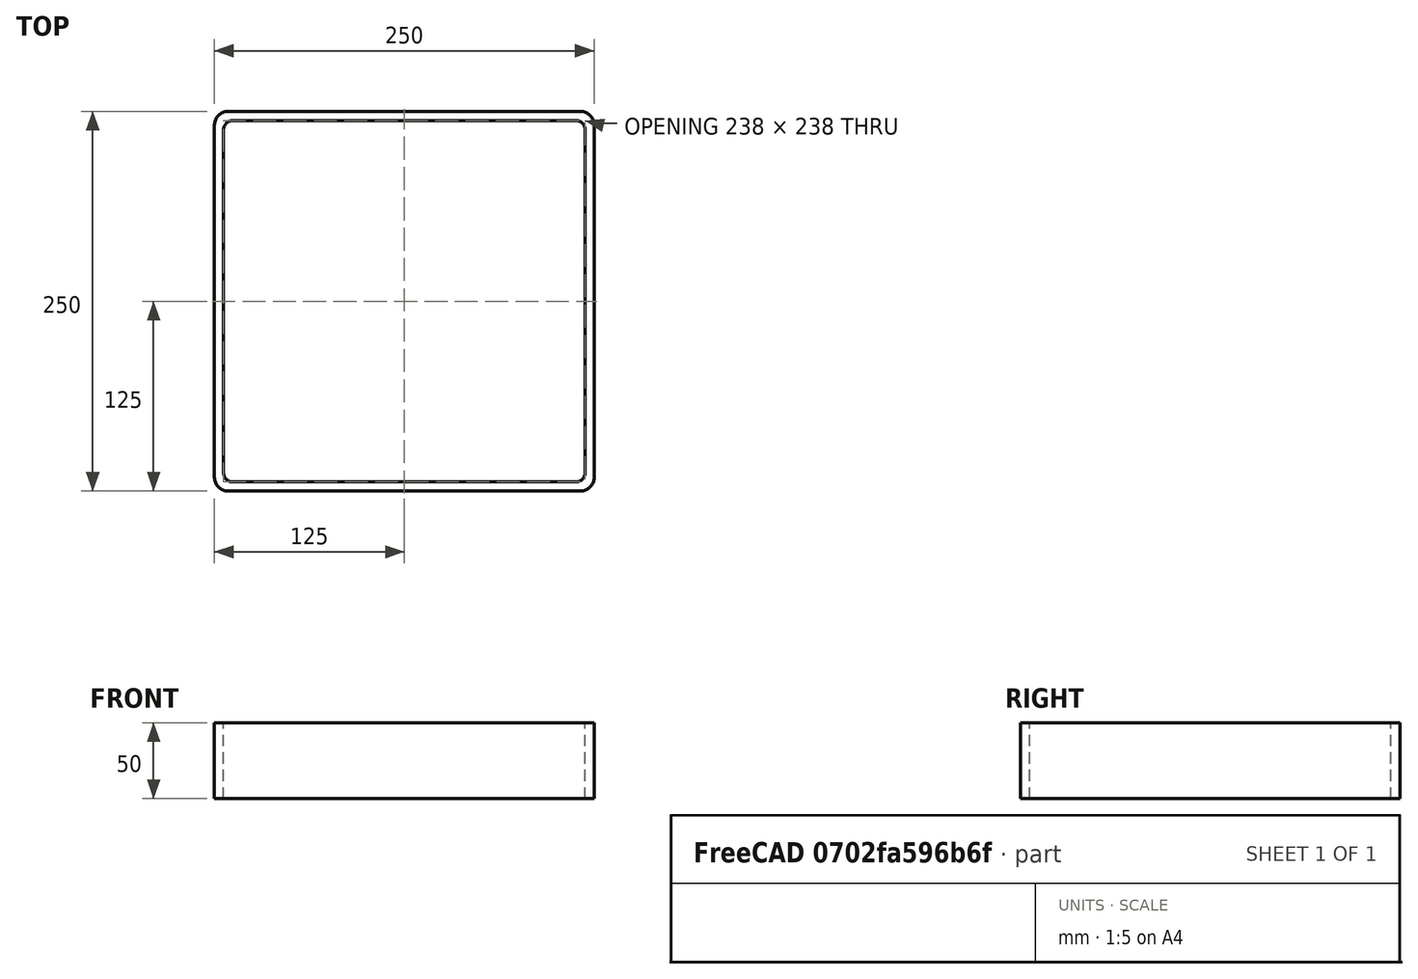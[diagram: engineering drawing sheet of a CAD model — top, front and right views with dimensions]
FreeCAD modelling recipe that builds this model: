
FCSTD DOCUMENT  (FreeCAD 0.15R4671 (Git))
Label: Square hollow section 250x250x6 EN10219 S235JRH
License: All rights reserved
LicenseURL: http://en.wikipedia.org/wiki/All_rights_reserved
objects: Sketcher::SketchObject×1, Part::Extrusion×1
note: 2 computed .brp shape members not serialized (recipe doc carries the construction recipe); baked Part::Feature solids carry a one-line shape summary decoded from their .brp

FEATURE [Sketcher::SketchObject] Sketch
  sketch-geometry (16):
    g0: LineSegment StartX=-113 StartY=119 StartZ=0 EndX=113 EndY=119 EndZ=0
    g1: LineSegment StartX=119 StartY=113 StartZ=0 EndX=119 EndY=-113 EndZ=0
    g2: LineSegment StartX=113 StartY=-119 StartZ=0 EndX=-113 EndY=-119 EndZ=0
    g3: LineSegment StartX=-119 StartY=-113 StartZ=0 EndX=-119 EndY=113 EndZ=0
    g4: LineSegment StartX=-116 StartY=125 StartZ=0 EndX=116 EndY=125 EndZ=0
    g5: LineSegment StartX=125 StartY=116 StartZ=0 EndX=125 EndY=-116 EndZ=0
    g6: LineSegment StartX=116 StartY=-125 StartZ=0 EndX=-116 EndY=-125 EndZ=0
    g7: LineSegment StartX=-125 StartY=-116 StartZ=0 EndX=-125 EndY=116 EndZ=0
    g8: ArcOfCircle CenterX=-113 CenterY=113 CenterZ=0 NormalX=0 NormalY=0 NormalZ=1 Radius=6 StartAngle=1.5708 EndAngle=3.14159
    g9: ArcOfCircle CenterX=113 CenterY=113 CenterZ=0 NormalX=0 NormalY=0 NormalZ=1 Radius=6 StartAngle=0 EndAngle=1.5708
    g10: ArcOfCircle CenterX=113 CenterY=-113 CenterZ=0 NormalX=0 NormalY=0 NormalZ=1 Radius=6 StartAngle=4.71239 EndAngle=6.28319
    g11: ArcOfCircle CenterX=-113 CenterY=-113 CenterZ=0 NormalX=0 NormalY=0 NormalZ=1 Radius=6 StartAngle=3.14159 EndAngle=4.71239
    g12: ArcOfCircle CenterX=116 CenterY=116 CenterZ=0 NormalX=0 NormalY=0 NormalZ=1 Radius=9 StartAngle=0 EndAngle=1.5708
    g13: ArcOfCircle CenterX=116 CenterY=-116 CenterZ=0 NormalX=0 NormalY=0 NormalZ=1 Radius=9 StartAngle=4.71239 EndAngle=6.28319
    g14: ArcOfCircle CenterX=-116 CenterY=-116 CenterZ=0 NormalX=0 NormalY=0 NormalZ=1 Radius=9 StartAngle=3.14159 EndAngle=4.71239
    g15: ArcOfCircle CenterX=-116 CenterY=116 CenterZ=0 NormalX=0 NormalY=0 NormalZ=1 Radius=9 StartAngle=1.5708 EndAngle=3.14159
  constraints (36):
    c: Horizontal(g2)
    c: Vertical(g3)
    c: Horizontal(g6)
    c: Vertical(g7)
    c: Tangent(g3,g8) = 1.5708
    c: Tangent(g0,g8) = 1.5708
    c: Tangent(g0,g9) = 1.5708
    c: Tangent(g1,g9) = 1.5708
    c: Tangent(g1,g10) = 1.5708
    c: Tangent(g2,g10) = 1.5708
    c: Tangent(g2,g11) = 1.5708
    c: Tangent(g3,g11) = 1.5708
    c: Tangent(g4,g12) = 1.5708
    c: Tangent(g5,g12) = 1.5708
    c: Tangent(g5,g13) = 1.5708
    c: Tangent(g6,g13) = 1.5708
    c: Tangent(g6,g14) = 1.5708
    c: Tangent(g7,g14) = 1.5708
    c: Tangent(g7,g15) = 1.5708
    c: Tangent(g4,g15) = 1.5708
    c: Equal(g9,g8)
    c: Equal(g9,g11)
    c: Equal(g9,g10)
    c: Equal(g12,g15)
    c: Equal(g12,g14)
    c: Equal(g12,g13)
    c: Symmetric(g4,g6,g-1)
    c: Symmetric(g7,g5,g-2)
    c: DistanceY(g4,g6) = -250
    c: DistanceX(g7,g5) = 250
    c: Symmetric(g3,g1,g-2)
    c: Symmetric(g0,g2,g-1)
    c: DistanceY(g0,g4) = 6
    c: DistanceX(g5,g1) = -6
    c: Radius(g9) = 6
    c: Radius(g12) = 9
FEATURE [Part::Extrusion] Extrude  label="Square hollow section 250x250x6 EN10219 S235JRH"
  Base = -> Sketch
  Dir = (0,0,50)
  Solid = true
